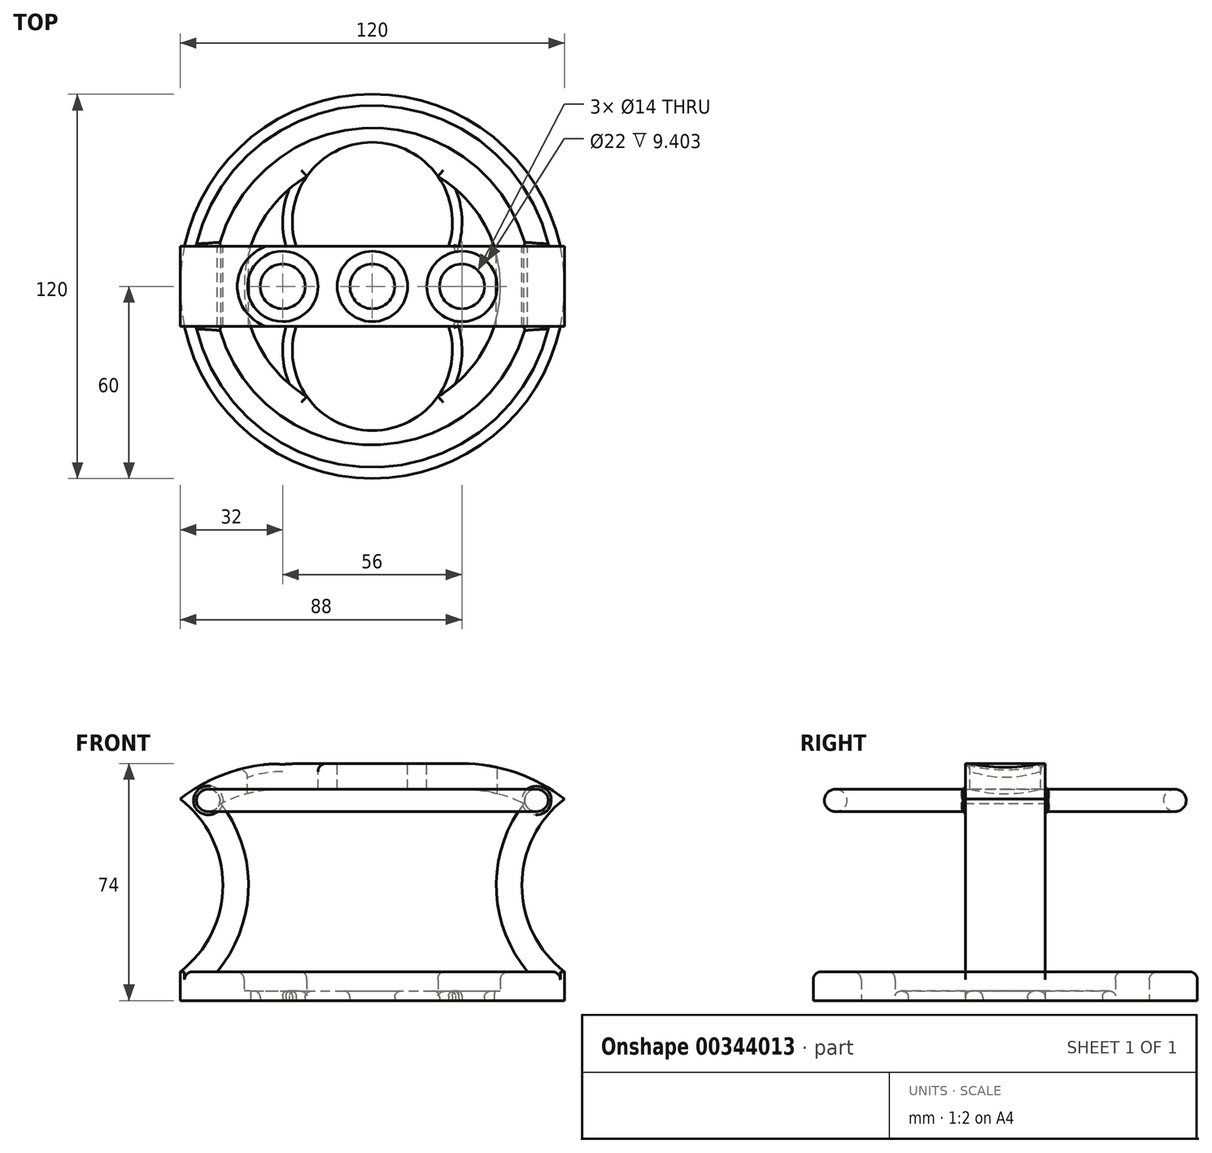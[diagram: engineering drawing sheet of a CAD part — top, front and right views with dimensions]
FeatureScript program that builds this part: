
annotation { "Feature Type Name" : "Feature", "Feature Type Description" : "" }
export const myFeature = defineFeature(function(context is Context, id is Id, definition is map)
    precondition{}
    {
        {
            var Q0;
            Q0=qCreatedBy(makeId("Front.planeOp"),FACE);
            var sketch = newSketch(context, id + "F0", { "sketchPlane" : qUnion([Q0])});
            skLineSegment(sketch, "E0.bottom", {"start": v(60, -4.5) * mm, "end": v(-60, -4.5) * mm});
            skLineSegment(sketch, "E0.top", {"start": v(60, 4.5) * mm, "end": v(-60, 4.5) * mm});
            skLineSegment(sketch, "E0.left", {"start": v(60, -4.5) * mm, "end": v(60, 4.5) * mm});
            skLineSegment(sketch, "E0.right", {"start": v(-60, -4.5) * mm, "end": v(-60, 4.5) * mm});
            skPoint(sketch, "E0.middle", {"position": v(0, 0) * mm});
            skLineSegment(sketch, "E1", {"start": v(0, 4.5) * mm, "end": v(0, -4.5) * mm});
            skLineSegment(sketch, "E2", {"start": v(-28, 69.5) * mm, "end": v(28, 69.5) * mm});
            skArc(sketch, "E3", {"start": v(60, 58.46) * mm, "mid": v(44.93, 66.66) * mm, "end": v(28, 69.5) * mm});
            skArc(sketch, "E4.MirrorCS", {"start": v(-60, 58.46) * mm, "mid": v(-44.93, 66.66) * mm, "end": v(-28, 69.5) * mm});
            skArc(sketch, "E5", {"start": v(-60, 4.5) * mm, "mid": v(-46.7, 31.48) * mm, "end": v(-60, 58.46) * mm});
            skArc(sketch, "E6.MirrorCS", {"start": v(60, 4.5) * mm, "mid": v(46.7, 31.48) * mm, "end": v(60, 58.46) * mm});
            skArc(sketch, "E7.0", {"start": v(48.5, 4.5) * mm, "mid": v(38.7, 30.55) * mm, "end": v(47.34, 57) * mm});
            skArc(sketch, "E7.1", {"start": v(-48.5, 4.5) * mm, "mid": v(-38.7, 30.55) * mm, "end": v(-47.34, 57) * mm});
            skArc(sketch, "E7.2", {"start": v(-47.34, 57) * mm, "mid": v(-37.93, 60.36) * mm, "end": v(-28, 61.5) * mm});
            skLineSegment(sketch, "E7.3", {"start": v(-28, 61.5) * mm, "end": v(28, 61.5) * mm});
            skArc(sketch, "E7.4", {"start": v(47.34, 57) * mm, "mid": v(37.93, 60.36) * mm, "end": v(28, 61.5) * mm});
            skSolve(sketch);
        }
        {
            var Q0;
            Q0=makeQuery(id+"F0.imprint","IMPRINT",FACE,{"disambiguationData":[TD([[makeQuery(id+"F0.imprint","IMPRINT",EDGE,{"derivedFrom":sQuery(id+"F0.wireOp",EDGE,"E2")}),-1.0]])]});
            extrude(context, id + "F1", {"entities" : qUnion([Q0]), "depth" : 25 * mm, "symmetric" : true});
        }
        {
            var Q0;
            {var subQ4=sQuery(id+"F0.wireOp",EDGE,"E0.left");Q0=makeQuery(id+"F0.imprint","IMPRINT",FACE,{"disambiguationData":[TD([[makeQuery(id+"F0.imprint","IMPRINT",EDGE,{"derivedFrom":subQ4}),1.0]])]});}
            var Q1;
            Q1=sQuery(id+"F0.wireOp",EDGE,"E1");
            revolve(context, id + "F2", {"operationType" : NewBodyOperationType.ADD, "entities" : qUnion([Q0]), "axis" : qUnion([Q1]), "revolveType" : RevolveType.FULL});
        }
        {
            var Q0;
            Q0=makeQuery(id+"F2.opRevolve","SWEPT_EDGE",EDGE,{"disambiguationData":[OSD([sQuery(id+"F0.wireOp",EDGE,"E0.top"),sQuery(id+"F0.wireOp",EDGE,"E0.left")])]});
            fillet(context, id + "F3", {"entities" : qUnion([Q0]), "radius" : 2.5 * mm, "tangentPropagation" : true, "allowEdgeOverflow" : false});
        }
        {
            var Q0;
            Q0=makeQuery(id+"F1.opExtrude","SWEPT_FACE",FACE,{"disambiguationData":[OSD([sQuery(id+"F0.wireOp",EDGE,"E2")])]});
            var sketch = newSketch(context, id + "F4", { "sketchPlane" : qUnion([Q0])});
            skCircle(sketch, "E8", {"center": v(0, 0) * mm, "radius": 11 * mm});
            skCircle(sketch, "E9", {"center": v(28, 0) * mm, "radius": 11 * mm});
            skCircle(sketch, "E10", {"center": v(-28, 0) * mm, "radius": 11 * mm});
            skSolve(sketch);
        }
        {
            var Q0;
            Q0 = qSketchRegion(id + "F4", true);
            extrude(context, id + "F5", {"entities" : qUnion([Q0]), "operationType" : NewBodyOperationType.REMOVE, "oppositeDirection" : true, "depth" : 25 * mm});
        }
        {
            var Q0;
            Q0=makeQuery(id+"F5.boolean.opBoolean","COPY",EDGE,{"derivedFrom":makeQuery(id+"F5.opExtrude","CAP_EDGE",EDGE,{"disambiguationData":[OSD([sQuery(id+"F4.wireOp",EDGE,"E10")])],"isStart":true})});
            var Q1;
            Q1=makeQuery(id+"F5.boolean.opBoolean","INTERSECT",EDGE,{"derivedFrom":[makeQuery(id+"F1.opExtrude","SWEPT_FACE",FACE,{"disambiguationData":[OSD([sQuery(id+"F0.wireOp",EDGE,"E4.MirrorCS")])]}),makeQuery(id+"F5.opExtrude","SWEPT_FACE",FACE,{"disambiguationData":[OSD([sQuery(id+"F4.wireOp",EDGE,"E10")])]})]});
            var Q2;
            Q2=makeQuery(id+"F5.boolean.opBoolean","COPY",EDGE,{"derivedFrom":makeQuery(id+"F5.opExtrude","CAP_EDGE",EDGE,{"disambiguationData":[OSD([sQuery(id+"F4.wireOp",EDGE,"E8")])],"isStart":true})});
            var Q3;
            Q3=makeQuery(id+"F5.boolean.opBoolean","COPY",EDGE,{"derivedFrom":makeQuery(id+"F5.opExtrude","CAP_EDGE",EDGE,{"disambiguationData":[OSD([sQuery(id+"F4.wireOp",EDGE,"E9")])],"isStart":true})});
            fillet(context, id + "F6", {"entities" : qUnion([Q0, Q1, Q2, Q3]), "radius" : 2.5 * mm, "tangentPropagation" : true, "allowEdgeOverflow" : false});
        }
        {
            var Q0;
            Q0=makeQuery(id+"F2.opRevolve","SWEPT_FACE",FACE,{"disambiguationData":[OSD([sQuery(id+"F0.wireOp",EDGE,"E0.bottom")])]});
            var sketch = newSketch(context, id + "F7", { "sketchPlane" : qUnion([Q0])});
            skArc(sketch, "E11", {"start": v(-20.45, 34.37) * mm, "mid": v(-40, 0) * mm, "end": v(-20.45, -34.38) * mm});
            skArc(sketch, "E12", {"start": v(20.45, 34.38) * mm, "mid": v(0, 45) * mm, "end": v(-20.45, 34.37) * mm});
            skArc(sketch, "E13.MirrorCS", {"start": v(20.45, -34.38) * mm, "mid": v(0, -45) * mm, "end": v(-20.45, -34.37) * mm});
            skArc(sketch, "E14.trimOffspring", {"start": v(20.45, -34.38) * mm, "mid": v(40, 0) * mm, "end": v(20.45, 34.38) * mm});
            skSolve(sketch);
        }
        {
            var Q0;
            Q0 = qSketchRegion(id + "F7", true);
            extrude(context, id + "F8", {"entities" : qUnion([Q0]), "operationType" : NewBodyOperationType.REMOVE, "oppositeDirection" : true, "depth" : 25 * mm});
        }
        {
            var Q0;
            Q0=makeQuery(id+"F8.boolean.opBoolean","INTERSECT",EDGE,{"derivedFrom":[makeQuery(id+"F2.opRevolve","SWEPT_FACE",FACE,{"disambiguationData":[OSD([sQuery(id+"F0.wireOp",EDGE,"E0.top")])]}),makeQuery(id+"F8.opExtrude","SWEPT_FACE",FACE,{"disambiguationData":[OSD([sQuery(id+"F7.wireOp",EDGE,"E11")])]})]});
            var Q1;
            Q1=makeQuery(id+"F8.boolean.opBoolean","INTERSECT",EDGE,{"derivedFrom":[makeQuery(id+"F2.opRevolve","SWEPT_FACE",FACE,{"disambiguationData":[OSD([sQuery(id+"F0.wireOp",EDGE,"E0.top")])]}),makeQuery(id+"F8.opExtrude","SWEPT_FACE",FACE,{"disambiguationData":[OSD([sQuery(id+"F7.wireOp",EDGE,"E13.MirrorCS")])]})]});
            var Q2;
            Q2=makeQuery(id+"F8.boolean.opBoolean","INTERSECT",EDGE,{"derivedFrom":[makeQuery(id+"F2.opRevolve","SWEPT_FACE",FACE,{"disambiguationData":[OSD([sQuery(id+"F0.wireOp",EDGE,"E0.top")])]}),makeQuery(id+"F8.opExtrude","SWEPT_FACE",FACE,{"disambiguationData":[OSD([sQuery(id+"F7.wireOp",EDGE,"E14.trimOffspring")])]})]});
            var Q3;
            Q3=makeQuery(id+"F8.boolean.opBoolean","INTERSECT",EDGE,{"derivedFrom":[makeQuery(id+"F2.opRevolve","SWEPT_FACE",FACE,{"disambiguationData":[OSD([sQuery(id+"F0.wireOp",EDGE,"E0.top")])]}),makeQuery(id+"F8.opExtrude","SWEPT_FACE",FACE,{"disambiguationData":[OSD([sQuery(id+"F7.wireOp",EDGE,"E12")])]})]});
            fillet(context, id + "F9", {"entities" : qUnion([Q0, Q1, Q2, Q3]), "radius" : 2.5 * mm, "tangentPropagation" : true, "allowEdgeOverflow" : false});
        }
        {
            var Q0;
            Q0=qCreatedBy(makeId("Front.planeOp"),FACE);
            var sketch = newSketch(context, id + "F10", { "sketchPlane" : qUnion([Q0])});
            skCircle(sketch, "E15", {"center": v(-53, 58) * mm, "radius": 3.5 * mm});
            skLineSegment(sketch, "E16", {"start": v(0, 62.67) * mm, "end": v(0, 37.39) * mm});
            skSolve(sketch);
        }
        {
            var Q0;
            Q0 = qSketchRegion(id + "F10", true);
            var Q1;
            Q1=sQuery(id+"F10.wireOp",EDGE,"E16");
            revolve(context, id + "F11", {"operationType" : NewBodyOperationType.ADD, "entities" : qUnion([Q0]), "axis" : qUnion([Q1]), "revolveType" : RevolveType.ONE_DIRECTION, "angle" : 360 * degree});
        }
        {
            var Q0;
            Q0=makeQuery(id+"F11.boolean.opBoolean","INTERSECT",EDGE,{"disambiguationData":[OD(1.0)],"derivedFrom":[makeQuery(id+"F1.opExtrude","CAP_FACE",FACE,{"disambiguationData":[OSD([sQuery(id+"F0.wireOp",EDGE,"E0.top"),sQuery(id+"F0.wireOp",EDGE,"E2"),sQuery(id+"F0.wireOp",EDGE,"E3"),sQuery(id+"F0.wireOp",EDGE,"E4.MirrorCS"),sQuery(id+"F0.wireOp",EDGE,"E5"),sQuery(id+"F0.wireOp",EDGE,"E6.MirrorCS"),sQuery(id+"F0.wireOp",EDGE,"E7.0"),sQuery(id+"F0.wireOp",EDGE,"E7.1"),sQuery(id+"F0.wireOp",EDGE,"E7.2"),sQuery(id+"F0.wireOp",EDGE,"E7.3"),sQuery(id+"F0.wireOp",EDGE,"E7.4")])],"isStart":true}),makeQuery(id+"F11.opRevolve","SWEPT_FACE",FACE,{"disambiguationData":[OSD([sQuery(id+"F10.wireOp",EDGE,"E15")])]})]});
            var Q1;
            Q1=makeQuery(id+"F11.boolean.opBoolean","INTERSECT",EDGE,{"disambiguationData":[OD(0.0)],"derivedFrom":[makeQuery(id+"F1.opExtrude","CAP_FACE",FACE,{"disambiguationData":[OSD([sQuery(id+"F0.wireOp",EDGE,"E0.top"),sQuery(id+"F0.wireOp",EDGE,"E2"),sQuery(id+"F0.wireOp",EDGE,"E3"),sQuery(id+"F0.wireOp",EDGE,"E4.MirrorCS"),sQuery(id+"F0.wireOp",EDGE,"E5"),sQuery(id+"F0.wireOp",EDGE,"E6.MirrorCS"),sQuery(id+"F0.wireOp",EDGE,"E7.0"),sQuery(id+"F0.wireOp",EDGE,"E7.1"),sQuery(id+"F0.wireOp",EDGE,"E7.2"),sQuery(id+"F0.wireOp",EDGE,"E7.3"),sQuery(id+"F0.wireOp",EDGE,"E7.4")])],"isStart":true}),makeQuery(id+"F11.opRevolve","SWEPT_FACE",FACE,{"disambiguationData":[OSD([sQuery(id+"F10.wireOp",EDGE,"E15")])]})]});
            var Q2;
            Q2=makeQuery(id+"F11.boolean.opBoolean","INTERSECT",EDGE,{"disambiguationData":[OD(0.0)],"derivedFrom":[makeQuery(id+"F1.opExtrude","CAP_FACE",FACE,{"disambiguationData":[OSD([sQuery(id+"F0.wireOp",EDGE,"E0.top"),sQuery(id+"F0.wireOp",EDGE,"E2"),sQuery(id+"F0.wireOp",EDGE,"E3"),sQuery(id+"F0.wireOp",EDGE,"E4.MirrorCS"),sQuery(id+"F0.wireOp",EDGE,"E5"),sQuery(id+"F0.wireOp",EDGE,"E6.MirrorCS"),sQuery(id+"F0.wireOp",EDGE,"E7.0"),sQuery(id+"F0.wireOp",EDGE,"E7.1"),sQuery(id+"F0.wireOp",EDGE,"E7.2"),sQuery(id+"F0.wireOp",EDGE,"E7.3"),sQuery(id+"F0.wireOp",EDGE,"E7.4")])],"isStart":false}),makeQuery(id+"F11.opRevolve","SWEPT_FACE",FACE,{"disambiguationData":[OSD([sQuery(id+"F10.wireOp",EDGE,"E15")])]})]});
            var Q3;
            Q3=makeQuery(id+"F11.boolean.opBoolean","INTERSECT",EDGE,{"disambiguationData":[OD(1.0)],"derivedFrom":[makeQuery(id+"F1.opExtrude","CAP_FACE",FACE,{"disambiguationData":[OSD([sQuery(id+"F0.wireOp",EDGE,"E0.top"),sQuery(id+"F0.wireOp",EDGE,"E2"),sQuery(id+"F0.wireOp",EDGE,"E3"),sQuery(id+"F0.wireOp",EDGE,"E4.MirrorCS"),sQuery(id+"F0.wireOp",EDGE,"E5"),sQuery(id+"F0.wireOp",EDGE,"E6.MirrorCS"),sQuery(id+"F0.wireOp",EDGE,"E7.0"),sQuery(id+"F0.wireOp",EDGE,"E7.1"),sQuery(id+"F0.wireOp",EDGE,"E7.2"),sQuery(id+"F0.wireOp",EDGE,"E7.3"),sQuery(id+"F0.wireOp",EDGE,"E7.4")])],"isStart":false}),makeQuery(id+"F11.opRevolve","SWEPT_FACE",FACE,{"disambiguationData":[OSD([sQuery(id+"F10.wireOp",EDGE,"E15")])]})]});
            fillet(context, id + "F12", {"entities" : qUnion([Q0, Q1, Q2, Q3]), "radius" : 1 * mm, "tangentPropagation" : true, "allowEdgeOverflow" : false});
        }
        {
            var Q0;
            Q0=makeQuery(id+"F7.imprint","IMPRINT",FACE,{"disambiguationData":[TD([[makeQuery(id+"F7.imprint","IMPRINT",EDGE,{"derivedFrom":sQuery(id+"F7.wireOp",EDGE,"E11")}),-1.0]])]});
            var sketch = newSketch(context, id + "F13", { "sketchPlane" : qUnion([Q0])});
            skLineSegment(sketch, "E17.0", {"start": v(-28, 12.5) * mm, "end": v(28, 12.5) * mm});
            skLineSegment(sketch, "E18.0", {"start": v(-28, -12.5) * mm, "end": v(28, -12.5) * mm});
            skArc(sketch, "E19.0", {"start": v(-38, 12.5) * mm, "mid": v(-40, 0) * mm, "end": v(-38, -12.5) * mm});
            skLineSegment(sketch, "E20", {"start": v(-28, 12.5) * mm, "end": v(-38, 12.5) * mm});
            skLineSegment(sketch, "E21", {"start": v(-38, 12.5) * mm, "end": v(28, 12.5) * mm});
            skLineSegment(sketch, "E22", {"start": v(-28, -12.5) * mm, "end": v(-38, -12.5) * mm});
            skLineSegment(sketch, "E23", {"start": v(-38, -12.5) * mm, "end": v(28, -12.5) * mm});
            skPoint(sketch, "E24.orphan", {"position": v(-20.45, -34.38) * mm});
            skPoint(sketch, "E25.orphan", {"position": v(-20.45, 34.37) * mm});
            skPoint(sketch, "E26.0.end.orphan", {"position": v(20.45, 34.38) * mm});
            skPoint(sketch, "E26.0.start.orphan", {"position": v(20.45, -34.38) * mm});
            skArc(sketch, "E27.0", {"start": v(38, -12.5) * mm, "mid": v(40, 0) * mm, "end": v(38, 12.5) * mm});
            skLineSegment(sketch, "E28", {"start": v(28, 12.5) * mm, "end": v(38, 12.5) * mm});
            skLineSegment(sketch, "E29", {"start": v(28, -12.5) * mm, "end": v(38, -12.5) * mm});
            skCircle(sketch, "E30", {"center": v(0, 0) * mm, "radius": 7 * mm});
            skCircle(sketch, "E31", {"center": v(28, 0) * mm, "radius": 7 * mm});
            skCircle(sketch, "E32", {"center": v(-28, 0) * mm, "radius": 7 * mm});
            skArc(sketch, "E33", {"start": v(23.85, 12.5) * mm, "mid": v(0, 45) * mm, "end": v(-23.85, 12.5) * mm});
            skPoint(sketch, "E33.third.point", {"position": v(0, 45) * mm});
            skArc(sketch, "E34.MirrorC", {"start": v(23.85, -12.5) * mm, "mid": v(0, -45) * mm, "end": v(-23.85, -12.5) * mm});
            skArc(sketch, "E35.0", {"start": v(26.71, 11.6) * mm, "mid": v(0, 48) * mm, "end": v(-26.71, 11.6) * mm});
            skArc(sketch, "E36.0", {"start": v(26.71, -11.6) * mm, "mid": v(0, -48) * mm, "end": v(-26.71, -11.6) * mm});
            skSolve(sketch);
        }
        {
            var Q0;
            Q0 = qSketchRegion(id + "F13", true);
            extrude(context, id + "F14", {"entities" : qUnion([Q0]), "operationType" : NewBodyOperationType.ADD, "oppositeDirection" : true, "depth" : 3 * mm});
        }
        {
            var Q0;
            Q0=makeQuery(id+"F14.opExtrude","CAP_EDGE",EDGE,{"disambiguationData":[OSD([sQuery(id+"F13.wireOp",EDGE,"E32")])],"isStart":false});
            var Q1;
            Q1=makeQuery(id+"F14.opExtrude","CAP_EDGE",EDGE,{"disambiguationData":[OSD([sQuery(id+"F13.wireOp",EDGE,"E30")])],"isStart":false});
            var Q2;
            Q2=makeQuery(id+"F14.opExtrude","CAP_EDGE",EDGE,{"disambiguationData":[OSD([sQuery(id+"F13.wireOp",EDGE,"E31")])],"isStart":false});
            var Q3;
            Q3=makeQuery(id+"F14.opExtrude","CAP_EDGE",EDGE,{"disambiguationData":[OSD([sQuery(id+"F13.wireOp",EDGE,"E21"),sQuery(id+"F13.wireOp",EDGE,"E28")])],"isStart":false});
            var Q4;
            {var subQ0=sQuery(id+"F13.wireOp",EDGE,"E33");var subQ1=sQuery(id+"F13.wireOp",EDGE,"E21");Q4=makeQuery(id+"F14.opExtrude","CAP_EDGE",EDGE,{"disambiguationData":[OSD([subQ1]),TDD([makeQuery(id+"F13.imprint","IMPRINT",EDGE,{"disambiguationData":[TD([[makeQuery(id+"F13.imprint","INTERSECT",VERTEX,{"disambiguationData":[OD(0.0)],"derivedFrom":[subQ1,subQ0]}),1.0]])],"derivedFrom":subQ1})])],"isStart":false});}
            var Q5;
            {var subQ0=sQuery(id+"F13.wireOp",EDGE,"E21");Q5=makeQuery(id+"F14.opExtrude","CAP_EDGE",EDGE,{"disambiguationData":[OSD([subQ0]),TDD([makeQuery(id+"F13.imprint","IMPRINT",EDGE,{"disambiguationData":[TD([[makeQuery(id+"F13.imprint","INTERSECT",VERTEX,{"disambiguationData":[OD(0.0)],"derivedFrom":[subQ0,sQuery(id+"F13.wireOp",EDGE,"E35.0")]}),1.0]])],"derivedFrom":subQ0})])],"isStart":false});}
            var Q6;
            {var subQ0=sQuery(id+"F13.wireOp",EDGE,"E23");Q6=makeQuery(id+"F14.opExtrude","CAP_EDGE",EDGE,{"disambiguationData":[OSD([subQ0]),TDD([makeQuery(id+"F13.imprint","IMPRINT",EDGE,{"disambiguationData":[TD([[makeQuery(id+"F13.imprint","INTERSECT",VERTEX,{"disambiguationData":[OD(0.0)],"derivedFrom":[subQ0,sQuery(id+"F13.wireOp",EDGE,"E36.0")]}),1.0]])],"derivedFrom":subQ0})])],"isStart":false});}
            var Q7;
            {var subQ0=sQuery(id+"F13.wireOp",EDGE,"E34.MirrorC");var subQ1=sQuery(id+"F13.wireOp",EDGE,"E23");Q7=makeQuery(id+"F14.opExtrude","CAP_EDGE",EDGE,{"disambiguationData":[OSD([subQ1]),TDD([makeQuery(id+"F13.imprint","IMPRINT",EDGE,{"disambiguationData":[TD([[makeQuery(id+"F13.imprint","INTERSECT",VERTEX,{"disambiguationData":[OD(0.0)],"derivedFrom":[subQ1,subQ0]}),-1.0]])],"derivedFrom":subQ1})])],"isStart":false});}
            var Q8;
            Q8=makeQuery(id+"F14.opExtrude","CAP_EDGE",EDGE,{"disambiguationData":[OSD([sQuery(id+"F13.wireOp",EDGE,"E23"),sQuery(id+"F13.wireOp",EDGE,"E29")])],"isStart":false});
            fillet(context, id + "F15", {"entities" : qUnion([Q0, Q1, Q2, Q3, Q4, Q5, Q6, Q7, Q8]), "radius" : 2 * mm, "tangentPropagation" : true, "allowEdgeOverflow" : false});
        }
        {
            var Q0;
            {var subQ0=sQuery(id+"F7.wireOp",EDGE,"E11");var subQ3=sQuery(id+"F13.wireOp",EDGE,"E36.0");Q0=makeQuery(id+"F14.boolean.opBoolean","SPLIT",EDGE,{"disambiguationData":[TD([makeQuery(id+"F8.boolean.opBoolean","COPY",FACE,{"derivedFrom":makeQuery(id+"F8.opExtrude","SWEPT_FACE",FACE,{"disambiguationData":[OSD([subQ0])]})})])],"derivedFrom":makeQuery(id+"F14.opExtrude","CAP_EDGE",EDGE,{"disambiguationData":[OSD([subQ3])],"isStart":false})});}
            var Q1;
            {var subQ0=sQuery(id+"F13.wireOp",EDGE,"E34.MirrorC");Q1=makeQuery(id+"F14.boolean.opBoolean","SPLIT",EDGE,{"disambiguationData":[TD([makeQuery(id+"F8.boolean.opBoolean","COPY",FACE,{"derivedFrom":makeQuery(id+"F8.opExtrude","SWEPT_FACE",FACE,{"disambiguationData":[OSD([sQuery(id+"F7.wireOp",EDGE,"E11")])]})})])],"derivedFrom":makeQuery(id+"F14.opExtrude","CAP_EDGE",EDGE,{"disambiguationData":[OSD([subQ0])],"isStart":false})});}
            var Q2;
            {var subQ0=sQuery(id+"F13.wireOp",EDGE,"E34.MirrorC");Q2=makeQuery(id+"F14.boolean.opBoolean","SPLIT",EDGE,{"disambiguationData":[TD([makeQuery(id+"F8.boolean.opBoolean","COPY",FACE,{"derivedFrom":makeQuery(id+"F8.opExtrude","SWEPT_FACE",FACE,{"disambiguationData":[OSD([sQuery(id+"F7.wireOp",EDGE,"E14.trimOffspring")])]})})])],"derivedFrom":makeQuery(id+"F14.opExtrude","CAP_EDGE",EDGE,{"disambiguationData":[OSD([subQ0])],"isStart":false})});}
            var Q3;
            {var subQ0=sQuery(id+"F13.wireOp",EDGE,"E36.0");Q3=makeQuery(id+"F14.boolean.opBoolean","SPLIT",EDGE,{"disambiguationData":[TD([makeQuery(id+"F8.boolean.opBoolean","COPY",FACE,{"derivedFrom":makeQuery(id+"F8.opExtrude","SWEPT_FACE",FACE,{"disambiguationData":[OSD([sQuery(id+"F7.wireOp",EDGE,"E14.trimOffspring")])]})})])],"derivedFrom":makeQuery(id+"F14.opExtrude","CAP_EDGE",EDGE,{"disambiguationData":[OSD([subQ0])],"isStart":false})});}
            var Q4;
            {var subQ0=sQuery(id+"F13.wireOp",EDGE,"E33");Q4=makeQuery(id+"F14.boolean.opBoolean","SPLIT",EDGE,{"disambiguationData":[TD([makeQuery(id+"F8.boolean.opBoolean","COPY",FACE,{"derivedFrom":makeQuery(id+"F8.opExtrude","SWEPT_FACE",FACE,{"disambiguationData":[OSD([sQuery(id+"F7.wireOp",EDGE,"E14.trimOffspring")])]})})])],"derivedFrom":makeQuery(id+"F14.opExtrude","CAP_EDGE",EDGE,{"disambiguationData":[OSD([subQ0])],"isStart":false})});}
            var Q5;
            {var subQ0=sQuery(id+"F13.wireOp",EDGE,"E35.0");Q5=makeQuery(id+"F14.boolean.opBoolean","SPLIT",EDGE,{"disambiguationData":[TD([makeQuery(id+"F8.boolean.opBoolean","COPY",FACE,{"derivedFrom":makeQuery(id+"F8.opExtrude","SWEPT_FACE",FACE,{"disambiguationData":[OSD([sQuery(id+"F7.wireOp",EDGE,"E14.trimOffspring")])]})})])],"derivedFrom":makeQuery(id+"F14.opExtrude","CAP_EDGE",EDGE,{"disambiguationData":[OSD([subQ0])],"isStart":false})});}
            var Q6;
            {var subQ0=sQuery(id+"F13.wireOp",EDGE,"E33");Q6=makeQuery(id+"F14.boolean.opBoolean","SPLIT",EDGE,{"disambiguationData":[TD([makeQuery(id+"F8.boolean.opBoolean","COPY",FACE,{"derivedFrom":makeQuery(id+"F8.opExtrude","SWEPT_FACE",FACE,{"disambiguationData":[OSD([sQuery(id+"F7.wireOp",EDGE,"E11")])]})})])],"derivedFrom":makeQuery(id+"F14.opExtrude","CAP_EDGE",EDGE,{"disambiguationData":[OSD([subQ0])],"isStart":false})});}
            var Q7;
            {var subQ0=sQuery(id+"F7.wireOp",EDGE,"E11");var subQ1=sQuery(id+"F13.wireOp",EDGE,"E35.0");Q7=makeQuery(id+"F14.boolean.opBoolean","SPLIT",EDGE,{"disambiguationData":[TD([makeQuery(id+"F8.boolean.opBoolean","COPY",FACE,{"derivedFrom":makeQuery(id+"F8.opExtrude","SWEPT_FACE",FACE,{"disambiguationData":[OSD([subQ0])]})})])],"derivedFrom":makeQuery(id+"F14.opExtrude","CAP_EDGE",EDGE,{"disambiguationData":[OSD([subQ1])],"isStart":false})});}
            fillet(context, id + "F16", {"entities" : qUnion([Q0, Q1, Q2, Q3, Q4, Q5, Q6, Q7]), "radius" : 1.5 * mm, "tangentPropagation" : true, "allowEdgeOverflow" : false});
        }
    });
